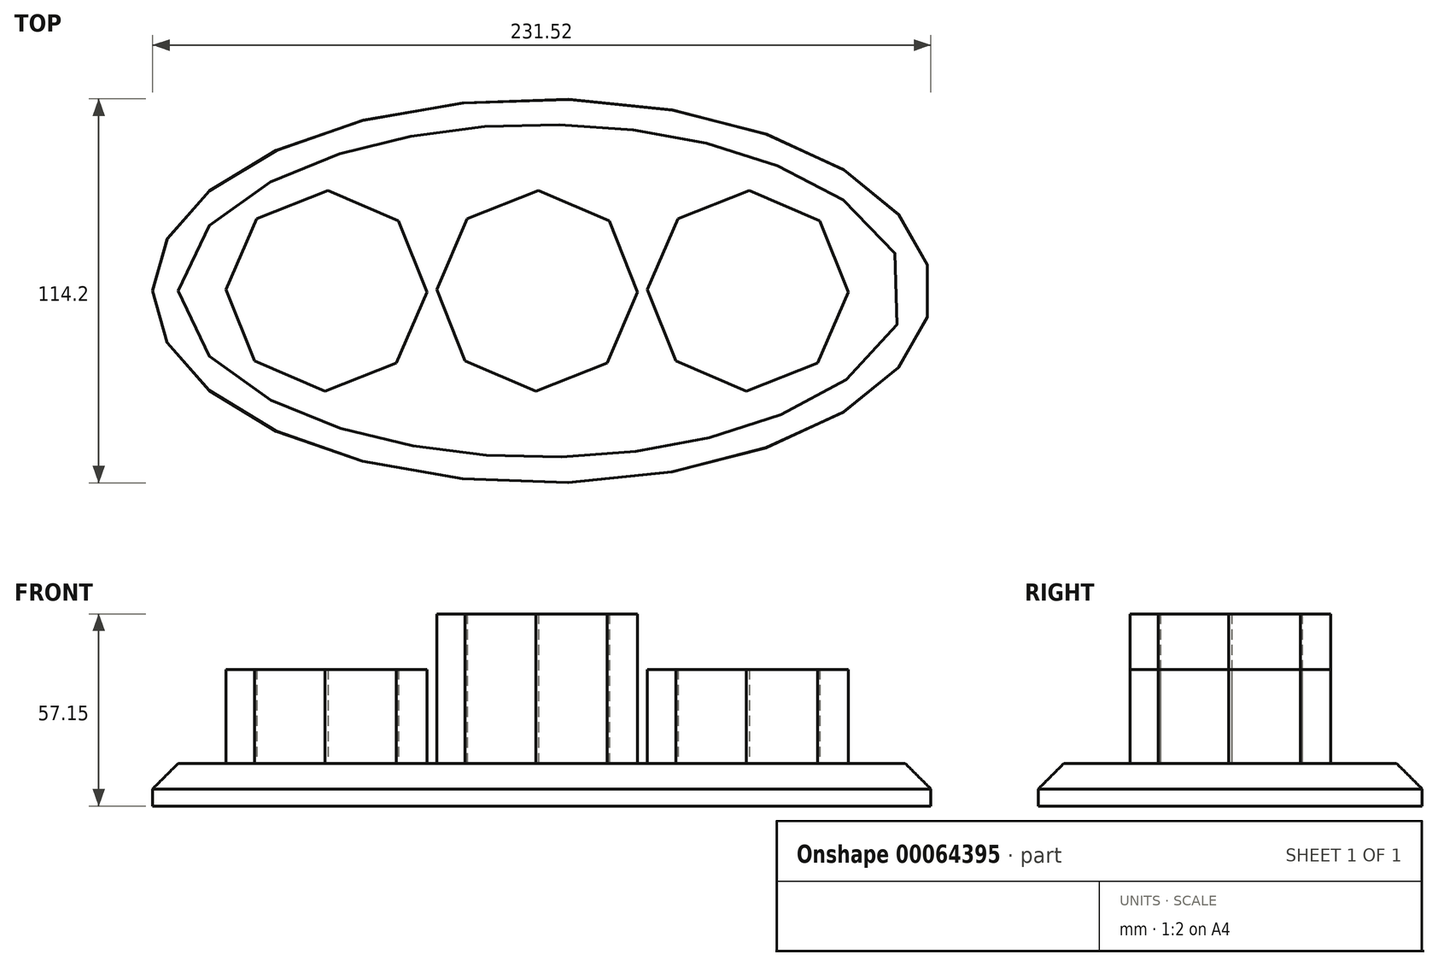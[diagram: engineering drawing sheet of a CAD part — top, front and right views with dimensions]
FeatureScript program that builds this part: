
annotation { "Feature Type Name" : "Feature", "Feature Type Description" : "" }
export const myFeature = defineFeature(function(context is Context, id is Id, definition is map)
    precondition{}
    {
        {
            var Q0;
            Q0=qCreatedBy(makeId("Top.planeOp"),FACE);
            var sketch = newSketch(context, id + "F0", { "sketchPlane" : qUnion([Q0])});
            skEllipse(sketch, "E0", {"center": v(0, 0) * mm, "majorRadius": 115.76 * mm, "minorRadius": 57.1 * mm, "majorAxis": v(-1, 0)});
            skSolve(sketch);
        }
        {
            var Q0;
            Q0 = qSketchRegion(id + "F0", true);
            extrude(context, id + "F1", {"entities" : qUnion([Q0]), "oppositeDirection" : true, "depth" : 12.7 * mm});
        }
        {
            var Q0;
            Q0=makeQuery(id+"F1.opExtrude","CAP_EDGE",EDGE,{"disambiguationData":[OSD([sQuery(id+"F0.wireOp",EDGE,"E0")])],"isStart":true});
            chamfer(context, id + "F2", {"entities" : qUnion([Q0]), "width" : 7.62 * mm});
        }
        {
            var Q0;
            Q0=makeQuery(id+"F1.opExtrude","CAP_FACE",FACE,{"disambiguationData":[OSD([sQuery(id+"F0.wireOp",EDGE,"E0")])],"isStart":true});
            var sketch = newSketch(context, id + "F3", { "sketchPlane" : qUnion([Q0])});
            skCircle(sketch, "E1.cCircle", {"center": v(61.3, 0) * mm, "radius": 29.87 * mm, "construction": true});
            skLineSegment(sketch, "E1.0", {"start": v(60.87, -29.86) * mm, "end": v(39.88, -20.81) * mm});
            skLineSegment(sketch, "E1.1", {"start": v(39.88, -20.81) * mm, "end": v(31.44, 0.43) * mm});
            skLineSegment(sketch, "E1.2", {"start": v(31.44, 0.43) * mm, "end": v(40.5, 21.42) * mm});
            skLineSegment(sketch, "E1.3", {"start": v(40.5, 21.42) * mm, "end": v(61.74, 29.86) * mm});
            skLineSegment(sketch, "E1.4", {"start": v(61.74, 29.86) * mm, "end": v(82.73, 20.81) * mm});
            skLineSegment(sketch, "E1.5", {"start": v(82.73, 20.81) * mm, "end": v(91.17, -0.43) * mm});
            skLineSegment(sketch, "E1.6", {"start": v(91.17, -0.43) * mm, "end": v(82.12, -21.42) * mm});
            skLineSegment(sketch, "E1.7", {"start": v(82.12, -21.42) * mm, "end": v(60.87, -29.86) * mm});
            skLineSegment(sketch, "E2.1.0.0", {"start": v(-31.22, 0.43) * mm, "end": v(-22.17, 21.42) * mm});
            skLineSegment(sketch, "E2.1.0.1", {"start": v(-22.17, 21.42) * mm, "end": v(-0.92, 29.86) * mm});
            skLineSegment(sketch, "E2.1.0.2", {"start": v(-0.92, 29.86) * mm, "end": v(20.07, 20.81) * mm});
            skLineSegment(sketch, "E2.1.0.3", {"start": v(20.07, 20.81) * mm, "end": v(28.5, -0.43) * mm});
            skLineSegment(sketch, "E2.1.0.4", {"start": v(28.5, -0.43) * mm, "end": v(19.45, -21.42) * mm});
            skLineSegment(sketch, "E2.1.0.5", {"start": v(19.45, -21.42) * mm, "end": v(-1.8, -29.86) * mm});
            skLineSegment(sketch, "E2.1.0.6", {"start": v(-1.8, -29.86) * mm, "end": v(-22.78, -20.81) * mm});
            skLineSegment(sketch, "E2.1.0.7", {"start": v(-22.78, -20.81) * mm, "end": v(-31.22, 0.43) * mm});
            skLineSegment(sketch, "E2.2.0.0", {"start": v(-93.89, 0.43) * mm, "end": v(-84.83, 21.42) * mm});
            skLineSegment(sketch, "E2.2.0.1", {"start": v(-84.83, 21.42) * mm, "end": v(-63.59, 29.86) * mm});
            skLineSegment(sketch, "E2.2.0.2", {"start": v(-63.59, 29.86) * mm, "end": v(-42.6, 20.81) * mm});
            skLineSegment(sketch, "E2.2.0.3", {"start": v(-42.6, 20.81) * mm, "end": v(-34.16, -0.43) * mm});
            skLineSegment(sketch, "E2.2.0.4", {"start": v(-34.16, -0.43) * mm, "end": v(-43.21, -21.42) * mm});
            skLineSegment(sketch, "E2.2.0.5", {"start": v(-43.21, -21.42) * mm, "end": v(-64.46, -29.86) * mm});
            skLineSegment(sketch, "E2.2.0.6", {"start": v(-64.46, -29.86) * mm, "end": v(-85.45, -20.81) * mm});
            skLineSegment(sketch, "E2.2.0.7", {"start": v(-85.45, -20.81) * mm, "end": v(-93.89, 0.43) * mm});
            skLineSegment(sketch, "E2.direction1", {"start": v(31.44, 0.43) * mm, "end": v(-31.22, 0.43) * mm, "construction": true});
            skLineSegment(sketch, "E3", {"start": v(-109.13, -67.13) * mm, "end": v(-109.13, 69.8) * mm, "construction": true});
            skLineSegment(sketch, "E4", {"start": v(107.67, -68.43) * mm, "end": v(107.67, 65.47) * mm, "construction": true});
            skSolve(sketch);
        }
        {
            var Q0;
            Q0=makeQuery(id+"F3.imprint","IMPRINT",FACE,{"disambiguationData":[TD([[makeQuery(id+"F3.imprint","IMPRINT",EDGE,{"derivedFrom":sQuery(id+"F3.wireOp",EDGE,"E2.1.0.0")}),-1.0]])]});
            extrude(context, id + "F4", {"entities" : qUnion([Q0]), "operationType" : NewBodyOperationType.ADD, "depth" : 44.45 * mm});
        }
        {
            var Q0;
            Q0=makeQuery(id+"F3.imprint","IMPRINT",FACE,{"disambiguationData":[TD([[makeQuery(id+"F3.imprint","IMPRINT",EDGE,{"derivedFrom":sQuery(id+"F3.wireOp",EDGE,"E2.2.0.0")}),-1.0]])]});
            var Q1;
            Q1=makeQuery(id+"F3.imprint","IMPRINT",FACE,{"disambiguationData":[TD([[makeQuery(id+"F3.imprint","IMPRINT",EDGE,{"derivedFrom":sQuery(id+"F3.wireOp",EDGE,"E1.0")}),-1.0]])]});
            extrude(context, id + "F5", {"entities" : qUnion([Q0, Q1]), "operationType" : NewBodyOperationType.ADD, "depth" : 27.94 * mm});
        }
    });
